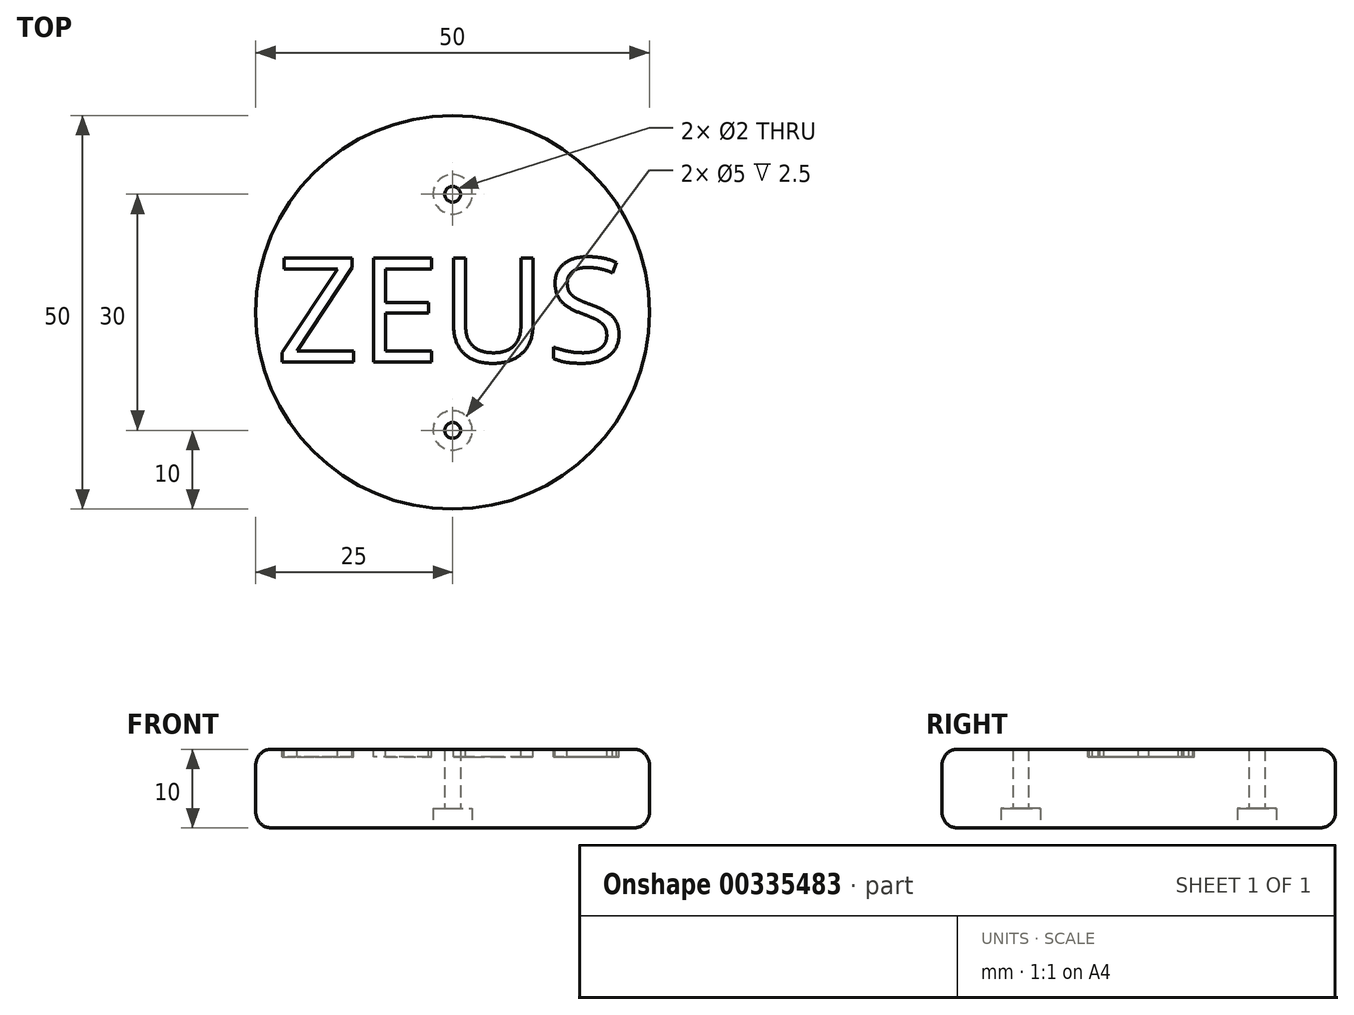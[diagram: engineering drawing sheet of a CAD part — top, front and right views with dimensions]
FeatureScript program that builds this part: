
annotation { "Feature Type Name" : "Feature", "Feature Type Description" : "" }
export const myFeature = defineFeature(function(context is Context, id is Id, definition is map)
    precondition{}
    {
        {
            var Q0;
            Q0=qCreatedBy(makeId("Top.planeOp"),FACE);
            var sketch = newSketch(context, id + "F0", { "sketchPlane" : qUnion([Q0])});
            skCircle(sketch, "E0", {"center": v(0, 0) * mm, "radius": 25 * mm});
            skSolve(sketch);
        }
        {
            var Q0;
            Q0=qSketchRegion(id+"F0",true);
            extrude(context, id + "F1", {"entities" : qUnion([Q0]), "depth" : 10 * mm});
        }
        {
            var Q0;
            Q0=makeQuery(id+"F1.opExtrude","CAP_FACE",FACE,{"disambiguationData":[OSD([sQuery(id+"F0.wireOp",EDGE,"E0")])],"isStart":false});
            var sketch = newSketch(context, id + "F2", { "sketchPlane" : qUnion([Q0])});
            skText(sketch, "E1", { "text": "ZEUS", "fontName": "OpenSans-Regular.ttf"});
            const initialGuessF2  = {"E1": [-0.02238, -0.0063, 1, 0, 0.0133]};
            skSetInitialGuess(sketch, initialGuessF2);
            skSolve(sketch);
        }
        {
            var Q0;
            Q0=qSketchRegion(id+"F2",true);
            extrude(context, id + "F3", {"entities" : qUnion([Q0]), "operationType" : NewBodyOperationType.REMOVE, "oppositeDirection" : true, "depth" : 1 * mm});
        }
        {
            var Q0;
            Q0=makeQuery(id+"F1.opExtrude","CAP_EDGE",EDGE,{"disambiguationData":[OSD([sQuery(id+"F0.wireOp",EDGE,"E0")])],"isStart":false});
            var Q1;
            Q1=makeQuery(id+"F1.opExtrude","CAP_EDGE",EDGE,{"disambiguationData":[OSD([sQuery(id+"F0.wireOp",EDGE,"E0")])],"isStart":true});
            fillet(context, id + "F4", {"entities" : qUnion([Q0, Q1]), "radius" : 2 * mm, "tangentPropagation" : true, "allowEdgeOverflow" : false});
        }
        {
            var Q0;
            Q0=makeQuery(id+"F1.opExtrude","CAP_FACE",FACE,{"disambiguationData":[OSD([sQuery(id+"F0.wireOp",EDGE,"E0")])],"isStart":true});
            var sketch = newSketch(context, id + "F5", { "sketchPlane" : qUnion([Q0])});
            skPoint(sketch, "E2", {"position": v(0, 15) * mm});
            skPoint(sketch, "E3", {"position": v(0, -15) * mm});
            skSolve(sketch);
        }
        {
            var Q0;
            Q0=sQuery(id+"F5.wireOp",VERTEX,"E2");
            var Q1;
            Q1=sQuery(id+"F5.wireOp",VERTEX,"E3");
            var Q2;
            Q2=makeQuery(id+"F1.opExtrude","SWEPT_BODY",BODY,{"disambiguationData":[OSD([sQuery(id+"F0.wireOp",EDGE,"E0")])]});
            hole(context, id + "F6", {"style" : HoleStyle.C_BORE, "endStyle" : HoleEndStyle.THROUGH, "holeDiameter" : 2 * mm, "cBoreDiameter" : 5 * mm, "cBoreDepth" : 2.5 * mm, "startFromSketch" : true, "locations" : qUnion([Q0, Q1]), "scope" : qUnion([Q2]), "isTappedThrough" : true});
        }
    });
